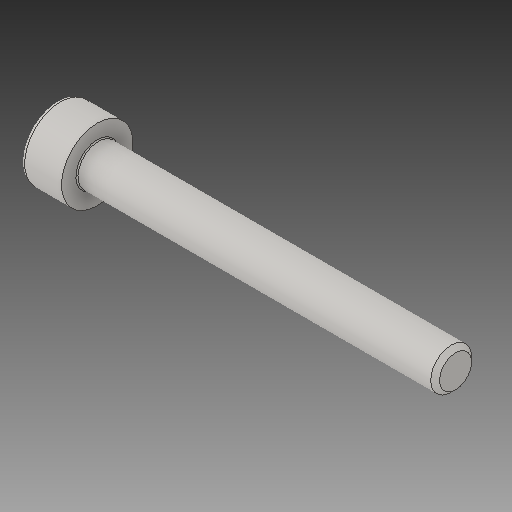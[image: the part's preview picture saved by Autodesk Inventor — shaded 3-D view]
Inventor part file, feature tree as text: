
AUTODESK INVENTOR PART (.ipt)
format: ipt  version: 2019 (Build 230136000, 136)  size: 117,760 bytes
history: imported  units: mm
features: imported_body x1
ambient origin geometry x8: Origin, YZ Plane, XZ Plane, XY Plane, X Axis, Y Axis, Z Axis, Center Point
bodies: Solide1 (imported_parasolid), Solid1 (imported_parasolid)
feature tree (1):
  imported_body  NMx_Import_Brep_tag  [imported B-rep: ~11 faces, bbox_mm=[38.6, 5.5, 0.0]]
